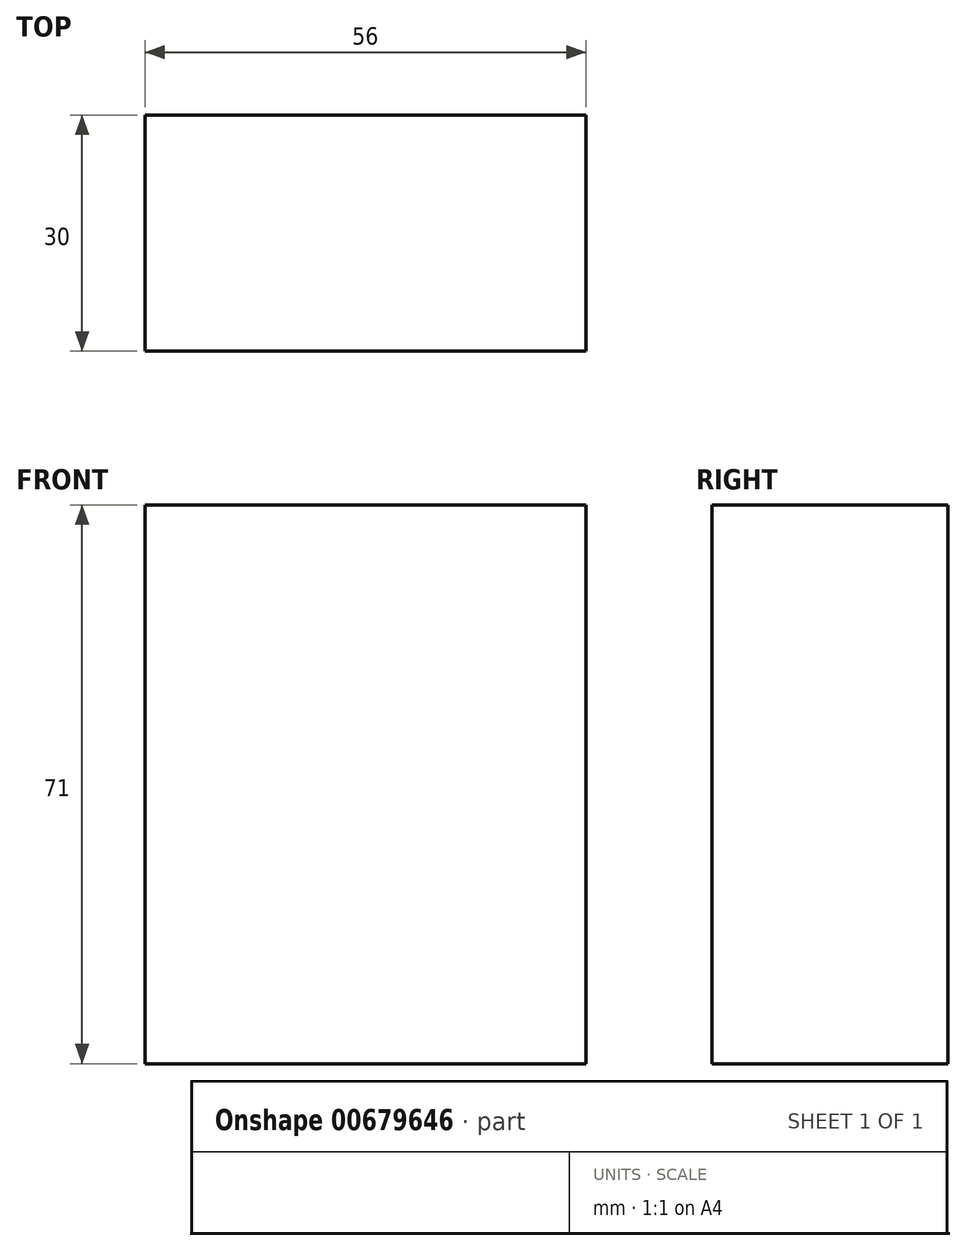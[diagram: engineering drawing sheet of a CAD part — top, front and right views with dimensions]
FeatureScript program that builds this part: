
annotation { "Feature Type Name" : "Feature", "Feature Type Description" : "" }
export const myFeature = defineFeature(function(context is Context, id is Id, definition is map)
    precondition{}
    {
        {
            var Q0;
            Q0=qCreatedBy(makeId("Top.planeOp"),FACE);
            var sketch = newSketch(context, id + "F0", { "sketchPlane" : qUnion([Q0])});
            skLineSegment(sketch, "E0.bottom", {"start": v(28, -15) * mm, "end": v(-28, -15) * mm});
            skLineSegment(sketch, "E0.top", {"start": v(28, 15) * mm, "end": v(-28, 15) * mm});
            skLineSegment(sketch, "E0.left", {"start": v(28, -15) * mm, "end": v(28, 15) * mm});
            skLineSegment(sketch, "E0.right", {"start": v(-28, -15) * mm, "end": v(-28, 15) * mm});
            skPoint(sketch, "E0.middle", {"position": v(0, 0) * mm});
            skSolve(sketch);
        }
        {
            var Q0;
            Q0=makeQuery(id+"F0.imprint","IMPRINT",FACE,{"disambiguationData":[TD([[makeQuery(id+"F0.imprint","IMPRINT",EDGE,{"derivedFrom":sQuery(id+"F0.wireOp",EDGE,"E0.bottom")}),-1.0]])]});
            extrude(context, id + "F1", {"entities" : qUnion([Q0]), "depth" : 71 * mm, "offsetDistance" : 25 * mm});
        }
        {
            var Q0;
            Q0=makeQuery(id+"F1.opExtrude","SWEPT_FACE",FACE,{"disambiguationData":[OSD([sQuery(id+"F0.wireOp",EDGE,"E0.bottom")])]});
            var sketch = newSketch(context, id + "F2", { "sketchPlane" : qUnion([Q0])});
            skLineSegment(sketch, "E1", {"start": v(-28, 15) * mm, "end": v(28, 15) * mm, "construction": true});
            skCircle(sketch, "E2", {"center": v(0, 43) * mm, "radius": 28 * mm});
            skPoint(sketch, "E2.centerSnap0", {"position": v(0, 15) * mm});
            skSolve(sketch);
        }
    });
